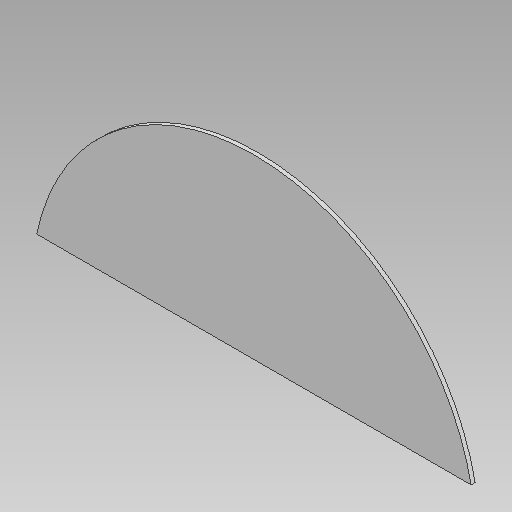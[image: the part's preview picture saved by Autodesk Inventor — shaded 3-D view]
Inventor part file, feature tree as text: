
AUTODESK INVENTOR PART (.ipt)
format: ipt  version: 2021 (Build 250183000, 183)  size: 96,768 bytes
history: native  units: mm
features: extrude x1, sketch x1
ambient origin geometry x8: Origin, YZ Plane, XZ Plane, XY Plane, X Axis, Y Axis, Z Axis, Center Point
bodies: Body1 (feature_tree)
feature tree (2):
  extrude  "side"  TaperAngle=0.0deg  [1 undecoded]
  sketch  "Sketch2"  dims[d14=20.0mm d15=0.0mm d17=0.0mm d21=0.0mm d24=890.0mm d25=2180.0mm d26=1090.0mm]
note: 1 required parameter value undecoded (feature->parameter linkage not recoverable at this tier; creation-order binding heuristic only, values carry confidence <= 0.55)
